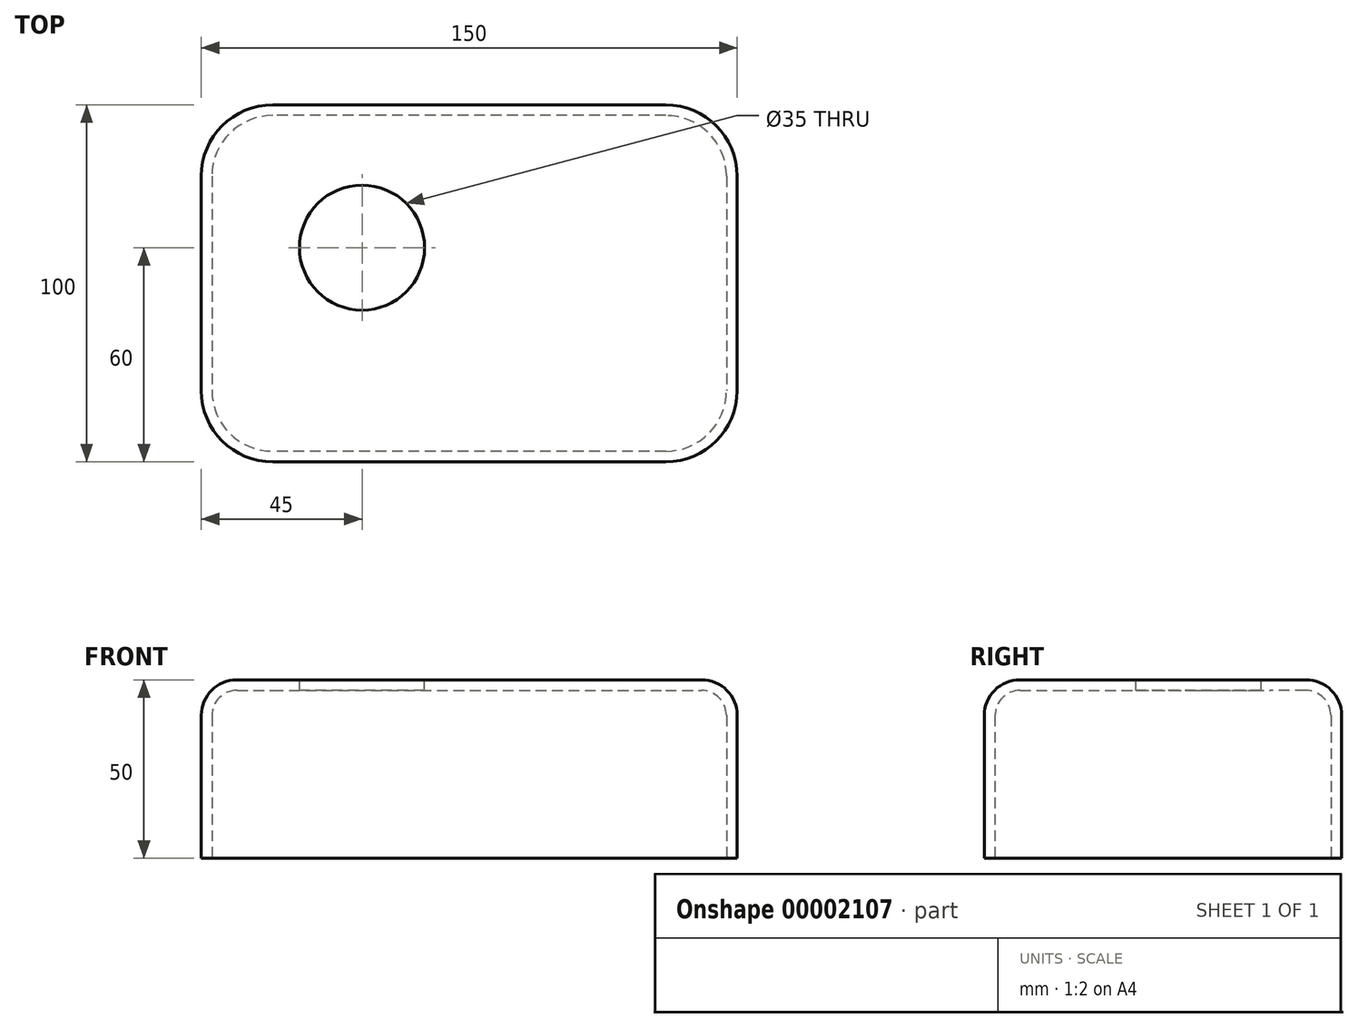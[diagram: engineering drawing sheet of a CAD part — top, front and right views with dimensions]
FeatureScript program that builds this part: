
annotation { "Feature Type Name" : "Feature", "Feature Type Description" : "" }
export const myFeature = defineFeature(function(context is Context, id is Id, definition is map)
    precondition{}
    {
        {
            var Q0;
            Q0=qCreatedBy(makeId("Top.planeOp"),FACE);
            var sketch = newSketch(context, id + "F0", { "sketchPlane" : qUnion([Q0])});
            skLineSegment(sketch, "E0.rect.bottom", {"start": v(75, 50) * mm, "end": v(-75, 50) * mm});
            skLineSegment(sketch, "E0.rect.top", {"start": v(75, -50) * mm, "end": v(-75, -50) * mm});
            skLineSegment(sketch, "E0.rect.left", {"start": v(75, 50) * mm, "end": v(75, -50) * mm});
            skLineSegment(sketch, "E0.rect.right", {"start": v(-75, 50) * mm, "end": v(-75, -50) * mm});
            skPoint(sketch, "E0.rect.middle", {"position": v(0, 0) * mm});
            skSolve(sketch);
        }
        {
            var Q0;
            Q0=makeQuery(id+"F0.imprint","IMPRINT",FACE,{"disambiguationData":[TD([[makeQuery(id+"F0.imprint","IMPRINT",EDGE,{"derivedFrom":sQuery(id+"F0.wireOp",EDGE,"E0.rect.bottom")}),1.0]])]});
            extrude(context, id + "F1", {"entities" : qUnion([Q0]), "depth" : 50 * mm});
        }
        {
            var Q0;
            Q0=makeQuery(id+"F1.opExtrude","SWEPT_EDGE",EDGE,{"disambiguationData":[OSD([sQuery(id+"F0.wireOp",EDGE,"E0.rect.bottom"),sQuery(id+"F0.wireOp",EDGE,"E0.rect.right")])]});
            var Q1;
            Q1=makeQuery(id+"F1.opExtrude","SWEPT_EDGE",EDGE,{"disambiguationData":[OSD([sQuery(id+"F0.wireOp",EDGE,"E0.rect.top"),sQuery(id+"F0.wireOp",EDGE,"E0.rect.right")])]});
            var Q2;
            Q2=makeQuery(id+"F1.opExtrude","SWEPT_EDGE",EDGE,{"disambiguationData":[OSD([sQuery(id+"F0.wireOp",EDGE,"E0.rect.top"),sQuery(id+"F0.wireOp",EDGE,"E0.rect.left")])]});
            var Q3;
            Q3=makeQuery(id+"F1.opExtrude","SWEPT_EDGE",EDGE,{"disambiguationData":[OSD([sQuery(id+"F0.wireOp",EDGE,"E0.rect.bottom"),sQuery(id+"F0.wireOp",EDGE,"E0.rect.left")])]});
            fillet(context, id + "F2", {"entities" : qUnion([Q0, Q1, Q2, Q3]), "radius" : 20 * mm, "tangentPropagation" : true, "allowEdgeOverflow" : false});
        }
        {
            var Q0;
            Q0=makeQuery(id+"F1.opExtrude","CAP_FACE",FACE,{"disambiguationData":[OSD([sQuery(id+"F0.wireOp",EDGE,"E0.rect.bottom"),sQuery(id+"F0.wireOp",EDGE,"E0.rect.top"),sQuery(id+"F0.wireOp",EDGE,"E0.rect.left"),sQuery(id+"F0.wireOp",EDGE,"E0.rect.right")])],"isStart":false});
            fillet(context, id + "F3", {"entities" : qUnion([Q0]), "radius" : 10 * mm, "tangentPropagation" : true, "allowEdgeOverflow" : false});
        }
        {
            var Q0;
            Q0=makeQuery(id+"F1.opExtrude","CAP_FACE",FACE,{"disambiguationData":[OSD([sQuery(id+"F0.wireOp",EDGE,"E0.rect.bottom"),sQuery(id+"F0.wireOp",EDGE,"E0.rect.top"),sQuery(id+"F0.wireOp",EDGE,"E0.rect.left"),sQuery(id+"F0.wireOp",EDGE,"E0.rect.right")])],"isStart":true});
            shell(context, id + "F4", {"entities" : qUnion([Q0]), "thickness" : 3 * mm});
        }
        {
            var Q0;
            Q0=makeQuery(id+"F1.opExtrude","CAP_FACE",FACE,{"disambiguationData":[OSD([sQuery(id+"F0.wireOp",EDGE,"E0.rect.bottom"),sQuery(id+"F0.wireOp",EDGE,"E0.rect.top"),sQuery(id+"F0.wireOp",EDGE,"E0.rect.left"),sQuery(id+"F0.wireOp",EDGE,"E0.rect.right")])],"isStart":false});
            var sketch = newSketch(context, id + "F5", { "sketchPlane" : qUnion([Q0])});
            skCircle(sketch, "E1", {"center": v(-30, 10) * mm, "radius": 17.5 * mm});
            skSolve(sketch);
        }
        {
            var Q0;
            Q0=qSketchRegion(id+"F5",true);
            extrude(context, id + "F6", {"entities" : qUnion([Q0]), "operationType" : NewBodyOperationType.REMOVE, "endBound" : BoundingType.THROUGH_ALL, "oppositeDirection" : true, "depth" : 25 * mm});
        }
    });
